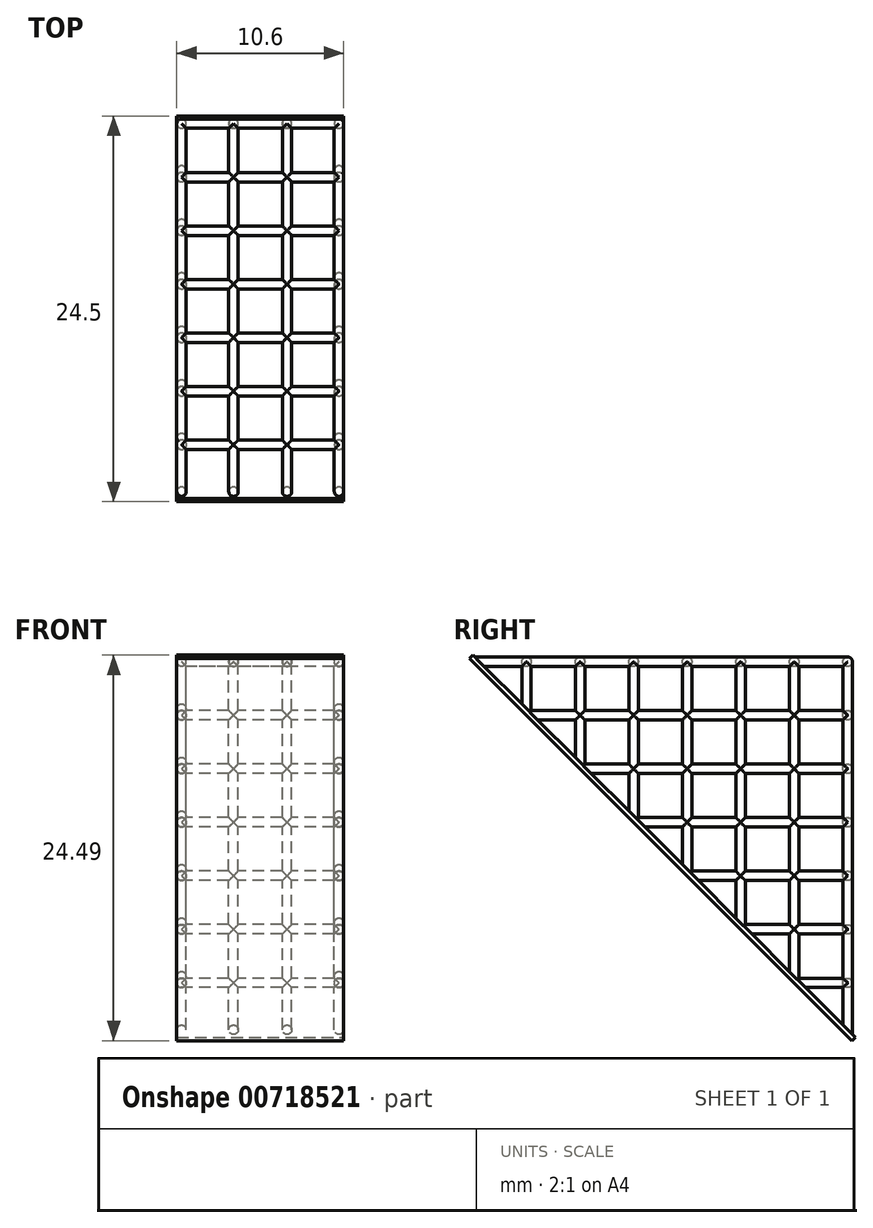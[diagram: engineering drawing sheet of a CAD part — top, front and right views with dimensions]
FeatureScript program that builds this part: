
annotation { "Feature Type Name" : "Feature", "Feature Type Description" : "" }
export const myFeature = defineFeature(function(context is Context, id is Id, definition is map)
    precondition{}
    {
        {
            var Q0;
            Q0=qCreatedBy(makeId("Top.planeOp"),FACE);
            cPlane(context, id + "F0", {"entities" : qUnion([Q0]), "cplaneType" : CPlaneType.OFFSET, "offset" : 0 * mm, "width" : 150 * mm, "height" : 150 * mm});
        }
        {
            var Q0;
            Q0=qCreatedBy(makeId("Front.planeOp"),FACE);
            cPlane(context, id + "F1", {"entities" : qUnion([Q0]), "cplaneType" : CPlaneType.OFFSET, "offset" : 0 * mm, "width" : 150 * mm, "height" : 150 * mm});
        }
        {
            assignVariable(context, id + "F2", {"variableType" : VariableType.LENGTH, "name" : "PoleD", "lengthValue" : 0.6 * mm});
        }
        {
            assignVariable(context, id + "F3", {"variableType" : VariableType.LENGTH, "name" : "PoleL", "lengthValue" : 10 * mm});
        }
        {
            assignVariable(context, id + "F4", {"variableType" : VariableType.LENGTH, "name" : "PoleL2", "lengthValue" : 23.8 * mm});
        }
        {
            var Q0;
            Q0=qCreatedBy(makeId("Right.planeOp"),FACE);
            var sketch = newSketch(context, id + "F5", { "sketchPlane" : qUnion([Q0])});
            skCircle(sketch, "E0", {"center": v(0, 0) * mm, "radius": 0.3 * mm});
            skCircle(sketch, "E1", {"center": v(3.4, 0) * mm, "radius": 0.3 * mm});
            skCircle(sketch, "E2", {"center": v(6.8, 0) * mm, "radius": 0.3 * mm});
            skCircle(sketch, "E3", {"center": v(10.2, 0) * mm, "radius": 0.3 * mm});
            skCircle(sketch, "E4", {"center": v(13.6, 0) * mm, "radius": 0.3 * mm});
            skCircle(sketch, "E5", {"center": v(17, 0) * mm, "radius": 0.3 * mm});
            skCircle(sketch, "E6", {"center": v(20.4, 0) * mm, "radius": 0.3 * mm});
            skCircle(sketch, "E7", {"center": v(23.8, 0) * mm, "radius": 0.3 * mm});
            skCircle(sketch, "E8", {"center": v(23.8, -3.4) * mm, "radius": 0.3 * mm});
            skCircle(sketch, "E9", {"center": v(23.8, -6.8) * mm, "radius": 0.3 * mm});
            skCircle(sketch, "E10", {"center": v(23.8, -10.2) * mm, "radius": 0.3 * mm});
            skCircle(sketch, "E11", {"center": v(23.8, -13.6) * mm, "radius": 0.3 * mm});
            skCircle(sketch, "E12", {"center": v(23.8, -17) * mm, "radius": 0.3 * mm});
            skCircle(sketch, "E13", {"center": v(23.8, -20.4) * mm, "radius": 0.3 * mm});
            skCircle(sketch, "E14", {"center": v(23.8, -23.8) * mm, "radius": 0.3 * mm});
            skSolve(sketch);
        }
        {
            var Q0;
            Q0 = qSketchRegion(id + "F5", true);
            extrude(context, id + "F6", {"entities" : qUnion([Q0]), "depth" : getVariable(context, 'PoleL'), "offsetDistance" : 25 * mm});
        }
        {
            var Q0;
            Q0=qCreatedBy(id+"F0.planeOp",FACE);
            var sketch = newSketch(context, id + "F7", { "sketchPlane" : qUnion([Q0])});
            skCircle(sketch, "E15", {"center": v(0, 0) * mm, "radius": 0.3 * mm});
            skCircle(sketch, "E16", {"center": v(0, 3.4) * mm, "radius": 0.3 * mm});
            skCircle(sketch, "E17", {"center": v(0, 6.8) * mm, "radius": 0.3 * mm});
            skCircle(sketch, "E18", {"center": v(0, 10.2) * mm, "radius": 0.3 * mm});
            skCircle(sketch, "E19", {"center": v(0, 13.6) * mm, "radius": 0.3 * mm});
            skCircle(sketch, "E20", {"center": v(0, 17) * mm, "radius": 0.3 * mm});
            skCircle(sketch, "E21", {"center": v(0, 20.4) * mm, "radius": 0.3 * mm});
            skCircle(sketch, "E22", {"center": v(0, 23.8) * mm, "radius": 0.3 * mm});
            skCircle(sketch, "E23", {"center": v(10, 0) * mm, "radius": 0.3 * mm});
            skCircle(sketch, "E24", {"center": v(10, 3.4) * mm, "radius": 0.3 * mm});
            skCircle(sketch, "E25", {"center": v(10, 6.8) * mm, "radius": 0.3 * mm});
            skCircle(sketch, "E26", {"center": v(10, 10.2) * mm, "radius": 0.3 * mm});
            skCircle(sketch, "E27", {"center": v(10, 13.6) * mm, "radius": 0.3 * mm});
            skCircle(sketch, "E28", {"center": v(10, 17) * mm, "radius": 0.3 * mm});
            skCircle(sketch, "E29", {"center": v(10, 20.4) * mm, "radius": 0.3 * mm});
            skCircle(sketch, "E30", {"center": v(3.3, 23.8) * mm, "radius": 0.3 * mm});
            skCircle(sketch, "E31", {"center": v(6.7, 23.8) * mm, "radius": 0.3 * mm});
            skCircle(sketch, "E32", {"center": v(10, 23.8) * mm, "radius": 0.3 * mm});
            skSolve(sketch);
        }
        {
            var Q0;
            Q0 = qSketchRegion(id + "F7", true);
            extrude(context, id + "F8", {"entities" : qUnion([Q0]), "oppositeDirection" : true, "depth" : getVariable(context, 'PoleL2'), "offsetDistance" : 25 * mm});
        }
        {
            var Q0;
            Q0=qCreatedBy(id+"F1.planeOp",FACE);
            var sketch = newSketch(context, id + "F9", { "sketchPlane" : qUnion([Q0])});
            skCircle(sketch, "E33", {"center": v(0, -23.8) * mm, "radius": 0.3 * mm});
            skCircle(sketch, "E34", {"center": v(0, -20.4) * mm, "radius": 0.3 * mm});
            skCircle(sketch, "E35", {"center": v(0, -17) * mm, "radius": 0.3 * mm});
            skCircle(sketch, "E36", {"center": v(0, -13.6) * mm, "radius": 0.3 * mm});
            skCircle(sketch, "E37", {"center": v(0, -10.2) * mm, "radius": 0.3 * mm});
            skCircle(sketch, "E38", {"center": v(0, -6.8) * mm, "radius": 0.3 * mm});
            skCircle(sketch, "E39", {"center": v(0, -3.4) * mm, "radius": 0.3 * mm});
            skCircle(sketch, "E40", {"center": v(0, 0) * mm, "radius": 0.3 * mm});
            skCircle(sketch, "E41", {"center": v(10, -23.8) * mm, "radius": 0.3 * mm});
            skCircle(sketch, "E42", {"center": v(10, -20.4) * mm, "radius": 0.3 * mm});
            skCircle(sketch, "E43", {"center": v(10, -17) * mm, "radius": 0.3 * mm});
            skCircle(sketch, "E44", {"center": v(10, -13.6) * mm, "radius": 0.3 * mm});
            skCircle(sketch, "E45", {"center": v(10, -10.2) * mm, "radius": 0.3 * mm});
            skCircle(sketch, "E46", {"center": v(10, -6.8) * mm, "radius": 0.3 * mm});
            skCircle(sketch, "E47", {"center": v(10, -3.4) * mm, "radius": 0.3 * mm});
            skCircle(sketch, "E48", {"center": v(3.3, 0) * mm, "radius": 0.3 * mm});
            skCircle(sketch, "E49", {"center": v(6.7, 0) * mm, "radius": 0.3 * mm});
            skCircle(sketch, "E50", {"center": v(10, 0) * mm, "radius": 0.3 * mm});
            skSolve(sketch);
        }
        {
            var Q0;
            Q0 = qSketchRegion(id + "F9", true);
            extrude(context, id + "F10", {"entities" : qUnion([Q0]), "oppositeDirection" : true, "depth" : getVariable(context, 'PoleL2'), "offsetDistance" : 25 * mm});
        }
        {
            var Q0;
            Q0=makeQuery(id+"F6.opExtrude","SWEPT_BODY",BODY,{"disambiguationData":[OSD([sQuery(id+"F5.wireOp",EDGE,"E6")])]});
            var Q1;
            Q1=makeQuery(id+"F6.opExtrude","SWEPT_BODY",BODY,{"disambiguationData":[OSD([sQuery(id+"F5.wireOp",EDGE,"E5")])]});
            var Q2;
            Q2=makeQuery(id+"F6.opExtrude","SWEPT_BODY",BODY,{"disambiguationData":[OSD([sQuery(id+"F5.wireOp",EDGE,"E4")])]});
            var Q3;
            Q3=makeQuery(id+"F6.opExtrude","SWEPT_BODY",BODY,{"disambiguationData":[OSD([sQuery(id+"F5.wireOp",EDGE,"E8")])]});
            var Q4;
            Q4=makeQuery(id+"F6.opExtrude","SWEPT_BODY",BODY,{"disambiguationData":[OSD([sQuery(id+"F5.wireOp",EDGE,"E3")])]});
            var Q5;
            Q5=makeQuery(id+"F6.opExtrude","SWEPT_BODY",BODY,{"disambiguationData":[OSD([sQuery(id+"F5.wireOp",EDGE,"E2")])]});
            var Q6;
            Q6=makeQuery(id+"F6.opExtrude","SWEPT_BODY",BODY,{"disambiguationData":[OSD([sQuery(id+"F5.wireOp",EDGE,"E9")])]});
            var Q7;
            Q7=makeQuery(id+"F6.opExtrude","SWEPT_BODY",BODY,{"disambiguationData":[OSD([sQuery(id+"F5.wireOp",EDGE,"E10")])]});
            var Q8;
            Q8=makeQuery(id+"F6.opExtrude","SWEPT_BODY",BODY,{"disambiguationData":[OSD([sQuery(id+"F5.wireOp",EDGE,"E11")])]});
            var Q9;
            Q9=makeQuery(id+"F6.opExtrude","SWEPT_BODY",BODY,{"disambiguationData":[OSD([sQuery(id+"F5.wireOp",EDGE,"E12")])]});
            var Q10;
            Q10=makeQuery(id+"F6.opExtrude","SWEPT_BODY",BODY,{"disambiguationData":[OSD([sQuery(id+"F5.wireOp",EDGE,"E13")])]});
            var Q11;
            Q11=makeQuery(id+"F6.opExtrude","SWEPT_BODY",BODY,{"disambiguationData":[OSD([sQuery(id+"F5.wireOp",EDGE,"E14")])]});
            var Q12;
            Q12=makeQuery(id+"F6.opExtrude","SWEPT_BODY",BODY,{"disambiguationData":[OSD([sQuery(id+"F5.wireOp",EDGE,"E1")])]});
            var Q13;
            Q13=makeQuery(id+"F8.opExtrude","SWEPT_BODY",BODY,{"disambiguationData":[OSD([sQuery(id+"F7.wireOp",EDGE,"E32")])]});
            var Q14;
            Q14=makeQuery(id+"F8.opExtrude","SWEPT_BODY",BODY,{"disambiguationData":[OSD([sQuery(id+"F7.wireOp",EDGE,"E31")])]});
            var Q15;
            Q15=makeQuery(id+"F8.opExtrude","SWEPT_BODY",BODY,{"disambiguationData":[OSD([sQuery(id+"F7.wireOp",EDGE,"E30")])]});
            var Q16;
            Q16=makeQuery(id+"F8.opExtrude","SWEPT_BODY",BODY,{"disambiguationData":[OSD([sQuery(id+"F7.wireOp",EDGE,"E29")])]});
            var Q17;
            Q17=makeQuery(id+"F8.opExtrude","SWEPT_BODY",BODY,{"disambiguationData":[OSD([sQuery(id+"F7.wireOp",EDGE,"E28")])]});
            var Q18;
            Q18=makeQuery(id+"F8.opExtrude","SWEPT_BODY",BODY,{"disambiguationData":[OSD([sQuery(id+"F7.wireOp",EDGE,"E27")])]});
            var Q19;
            Q19=makeQuery(id+"F8.opExtrude","SWEPT_BODY",BODY,{"disambiguationData":[OSD([sQuery(id+"F7.wireOp",EDGE,"E26")])]});
            var Q20;
            Q20=makeQuery(id+"F6.opExtrude","SWEPT_BODY",BODY,{"disambiguationData":[OSD([sQuery(id+"F5.wireOp",EDGE,"E0")])]});
            var Q21;
            Q21=makeQuery(id+"F8.opExtrude","SWEPT_BODY",BODY,{"disambiguationData":[OSD([sQuery(id+"F7.wireOp",EDGE,"E15")])]});
            var Q22;
            Q22=makeQuery(id+"F8.opExtrude","SWEPT_BODY",BODY,{"disambiguationData":[OSD([sQuery(id+"F7.wireOp",EDGE,"E25")])]});
            var Q23;
            Q23=makeQuery(id+"F8.opExtrude","SWEPT_BODY",BODY,{"disambiguationData":[OSD([sQuery(id+"F7.wireOp",EDGE,"E23")])]});
            var Q24;
            Q24=makeQuery(id+"F8.opExtrude","SWEPT_BODY",BODY,{"disambiguationData":[OSD([sQuery(id+"F7.wireOp",EDGE,"E24")])]});
            var Q25;
            Q25=makeQuery(id+"F8.opExtrude","SWEPT_BODY",BODY,{"disambiguationData":[OSD([sQuery(id+"F7.wireOp",EDGE,"E21")])]});
            var Q26;
            Q26=makeQuery(id+"F8.opExtrude","SWEPT_BODY",BODY,{"disambiguationData":[OSD([sQuery(id+"F7.wireOp",EDGE,"E22")])]});
            var Q27;
            Q27=makeQuery(id+"F8.opExtrude","SWEPT_BODY",BODY,{"disambiguationData":[OSD([sQuery(id+"F7.wireOp",EDGE,"E20")])]});
            var Q28;
            Q28=makeQuery(id+"F8.opExtrude","SWEPT_BODY",BODY,{"disambiguationData":[OSD([sQuery(id+"F7.wireOp",EDGE,"E19")])]});
            var Q29;
            Q29=makeQuery(id+"F8.opExtrude","SWEPT_BODY",BODY,{"disambiguationData":[OSD([sQuery(id+"F7.wireOp",EDGE,"E18")])]});
            var Q30;
            Q30=makeQuery(id+"F8.opExtrude","SWEPT_BODY",BODY,{"disambiguationData":[OSD([sQuery(id+"F7.wireOp",EDGE,"E17")])]});
            var Q31;
            Q31=makeQuery(id+"F6.opExtrude","SWEPT_BODY",BODY,{"disambiguationData":[OSD([sQuery(id+"F5.wireOp",EDGE,"E7")])]});
            var Q32;
            Q32=makeQuery(id+"F8.opExtrude","SWEPT_BODY",BODY,{"disambiguationData":[OSD([sQuery(id+"F7.wireOp",EDGE,"E16")])]});
            var Q33;
            Q33=makeQuery(id+"F10.opExtrude","SWEPT_BODY",BODY,{"disambiguationData":[OSD([sQuery(id+"F9.wireOp",EDGE,"E33")])]});
            var Q34;
            Q34=makeQuery(id+"F10.opExtrude","SWEPT_BODY",BODY,{"disambiguationData":[OSD([sQuery(id+"F9.wireOp",EDGE,"E34")])]});
            var Q35;
            Q35=makeQuery(id+"F10.opExtrude","SWEPT_BODY",BODY,{"disambiguationData":[OSD([sQuery(id+"F9.wireOp",EDGE,"E35")])]});
            var Q36;
            Q36=makeQuery(id+"F10.opExtrude","SWEPT_BODY",BODY,{"disambiguationData":[OSD([sQuery(id+"F9.wireOp",EDGE,"E36")])]});
            var Q37;
            Q37=makeQuery(id+"F10.opExtrude","SWEPT_BODY",BODY,{"disambiguationData":[OSD([sQuery(id+"F9.wireOp",EDGE,"E37")])]});
            var Q38;
            Q38=makeQuery(id+"F10.opExtrude","SWEPT_BODY",BODY,{"disambiguationData":[OSD([sQuery(id+"F9.wireOp",EDGE,"E38")])]});
            var Q39;
            Q39=makeQuery(id+"F10.opExtrude","SWEPT_BODY",BODY,{"disambiguationData":[OSD([sQuery(id+"F9.wireOp",EDGE,"E39")])]});
            var Q40;
            Q40=makeQuery(id+"F10.opExtrude","SWEPT_BODY",BODY,{"disambiguationData":[OSD([sQuery(id+"F9.wireOp",EDGE,"E40")])]});
            var Q41;
            Q41=makeQuery(id+"F10.opExtrude","SWEPT_BODY",BODY,{"disambiguationData":[OSD([sQuery(id+"F9.wireOp",EDGE,"E41")])]});
            var Q42;
            Q42=makeQuery(id+"F10.opExtrude","SWEPT_BODY",BODY,{"disambiguationData":[OSD([sQuery(id+"F9.wireOp",EDGE,"E42")])]});
            var Q43;
            Q43=makeQuery(id+"F10.opExtrude","SWEPT_BODY",BODY,{"disambiguationData":[OSD([sQuery(id+"F9.wireOp",EDGE,"E43")])]});
            var Q44;
            Q44=makeQuery(id+"F10.opExtrude","SWEPT_BODY",BODY,{"disambiguationData":[OSD([sQuery(id+"F9.wireOp",EDGE,"E44")])]});
            var Q45;
            Q45=makeQuery(id+"F10.opExtrude","SWEPT_BODY",BODY,{"disambiguationData":[OSD([sQuery(id+"F9.wireOp",EDGE,"E45")])]});
            var Q46;
            Q46=makeQuery(id+"F10.opExtrude","SWEPT_BODY",BODY,{"disambiguationData":[OSD([sQuery(id+"F9.wireOp",EDGE,"E46")])]});
            var Q47;
            Q47=makeQuery(id+"F10.opExtrude","SWEPT_BODY",BODY,{"disambiguationData":[OSD([sQuery(id+"F9.wireOp",EDGE,"E47")])]});
            var Q48;
            Q48=makeQuery(id+"F10.opExtrude","SWEPT_BODY",BODY,{"disambiguationData":[OSD([sQuery(id+"F9.wireOp",EDGE,"E48")])]});
            var Q49;
            Q49=makeQuery(id+"F10.opExtrude","SWEPT_BODY",BODY,{"disambiguationData":[OSD([sQuery(id+"F9.wireOp",EDGE,"E49")])]});
            var Q50;
            Q50=makeQuery(id+"F10.opExtrude","SWEPT_BODY",BODY,{"disambiguationData":[OSD([sQuery(id+"F9.wireOp",EDGE,"E50")])]});
            booleanBodies(context, id + "F11", {"operationType" : BooleanOperationType.UNION, "tools" : qUnion([Q0, Q1, Q2, Q3, Q4, Q5, Q6, Q7, Q8, Q9, Q10, Q11, Q12, Q13, Q14, Q15, Q16, Q17, Q18, Q19, Q20, Q21, Q22, Q23, Q24, Q25, Q26, Q27, Q28, Q29, Q30, Q31, Q32, Q33, Q34, Q35, Q36, Q37, Q38, Q39, Q40, Q41, Q42, Q43, Q44, Q45, Q46, Q47, Q48, Q49, Q50])});
        }
        {
            var Q0;
            Q0=makeQuery(id+"F8.opExtrude","CAP_FACE",FACE,{"disambiguationData":[OSD([sQuery(id+"F7.wireOp",EDGE,"E32")])],"isStart":true});
            var sketch = newSketch(context, id + "F12", { "sketchPlane" : qUnion([Q0])});
            skLineSegment(sketch, "E51", {"start": v(10, 23.8) * mm, "end": v(10, 24.35) * mm});
            skSolve(sketch);
        }
        {
            var Q0;
            Q0=makeQuery(id+"F8.opExtrude","CAP_FACE",FACE,{"disambiguationData":[OSD([sQuery(id+"F7.wireOp",EDGE,"E23")])],"isStart":true});
            var sketch = newSketch(context, id + "F13", { "sketchPlane" : qUnion([Q0])});
            skLineSegment(sketch, "E52", {"start": v(10, 0) * mm, "end": v(10, -0.38) * mm});
            skSolve(sketch);
        }
        {
            var Q0;
            {var subQ1=sQuery(id+"F7.wireOp",EDGE,"E23");var subQ2=makeQuery(id+"F8.opExtrude","CAP_EDGE",EDGE,{"disambiguationData":[OSD([subQ1])],"isStart":true});Q0=makeQuery(id+"F13.imprint","IMPRINT",FACE,{"disambiguationData":[TD([[makeQuery(id+"F13.imprint","IMPRINT",EDGE,{"derivedFrom":subQ2}),1.0]])]});}
            var Q1;
            Q1=sQuery(id+"F13.wireOp",EDGE,"E52");
            revolve(context, id + "F14", {"operationType" : NewBodyOperationType.ADD, "surfaceOperationType" : NewSurfaceOperationType.NEW, "entities" : qUnion([Q0]), "axis" : qUnion([Q1]), "revolveType" : RevolveType.FULL});
        }
        {
            var Q0;
            {var subQ1=sQuery(id+"F7.wireOp",EDGE,"E32");var subQ2=makeQuery(id+"F8.opExtrude","CAP_EDGE",EDGE,{"disambiguationData":[OSD([subQ1])],"isStart":true});Q0=makeQuery(id+"F12.imprint","IMPRINT",FACE,{"disambiguationData":[TD([[makeQuery(id+"F12.imprint","IMPRINT",EDGE,{"derivedFrom":subQ2}),1.0]])]});}
            var Q1;
            Q1=sQuery(id+"F12.wireOp",EDGE,"E51");
            revolve(context, id + "F15", {"operationType" : NewBodyOperationType.ADD, "surfaceOperationType" : NewSurfaceOperationType.NEW, "entities" : qUnion([Q0]), "axis" : qUnion([Q1]), "revolveType" : RevolveType.FULL});
        }
        {
            var Q0;
            Q0=makeQuery(id+"F8.opExtrude","CAP_FACE",FACE,{"disambiguationData":[OSD([sQuery(id+"F7.wireOp",EDGE,"E22")])],"isStart":true});
            var sketch = newSketch(context, id + "F16", { "sketchPlane" : qUnion([Q0])});
            skLineSegment(sketch, "E53", {"start": v(0, 23.8) * mm, "end": v(0, 24.59) * mm});
            skSolve(sketch);
        }
        {
            var Q0;
            Q0=makeQuery(id+"F6.opExtrude","CAP_FACE",FACE,{"disambiguationData":[OSD([sQuery(id+"F5.wireOp",EDGE,"E7")])],"isStart":true});
            var Q1;
            Q1=sQuery(id+"F16.wireOp",EDGE,"E53");
            revolve(context, id + "F17", {"operationType" : NewBodyOperationType.ADD, "surfaceOperationType" : NewSurfaceOperationType.NEW, "entities" : qUnion([Q0]), "axis" : qUnion([Q1]), "revolveType" : RevolveType.FULL});
        }
        {
            var Q0;
            Q0=makeQuery(id+"F10.opExtrude","CAP_FACE",FACE,{"disambiguationData":[OSD([sQuery(id+"F9.wireOp",EDGE,"E33")])],"isStart":false});
            var sketch = newSketch(context, id + "F18", { "sketchPlane" : qUnion([Q0])});
            skLineSegment(sketch, "E54", {"start": v(0, -23.8) * mm, "end": v(0.65, -23.8) * mm});
            skLineSegment(sketch, "E55", {"start": v(0.65, -23.8) * mm, "end": v(-11.19, -23.8) * mm});
            skSolve(sketch);
        }
        {
            var Q0;
            Q0=makeQuery(id+"F8.opExtrude","CAP_FACE",FACE,{"disambiguationData":[OSD([sQuery(id+"F7.wireOp",EDGE,"E32")])],"isStart":false});
            var Q1;
            Q1=sQuery(id+"F18.wireOp",EDGE,"E55");
            revolve(context, id + "F19", {"operationType" : NewBodyOperationType.ADD, "surfaceOperationType" : NewSurfaceOperationType.NEW, "entities" : qUnion([Q0]), "axis" : qUnion([Q1]), "revolveType" : RevolveType.FULL});
        }
        {
            var Q0;
            Q0=makeQuery(id+"F8.opExtrude","CAP_FACE",FACE,{"disambiguationData":[OSD([sQuery(id+"F7.wireOp",EDGE,"E22")])],"isStart":false});
            var Q1;
            Q1=makeQuery(id+"F11.opBoolean","INTERSECT",EDGE,{"derivedFrom":[makeQuery(id+"F8.opExtrude","CAP_FACE",FACE,{"disambiguationData":[OSD([sQuery(id+"F7.wireOp",EDGE,"E22")])],"isStart":false}),makeQuery(id+"F10.opExtrude","CAP_FACE",FACE,{"disambiguationData":[OSD([sQuery(id+"F9.wireOp",EDGE,"E33")])],"isStart":false})]});
            revolve(context, id + "F20", {"operationType" : NewBodyOperationType.ADD, "surfaceOperationType" : NewSurfaceOperationType.NEW, "entities" : qUnion([Q0]), "axis" : qUnion([Q1]), "revolveType" : RevolveType.FULL});
        }
        {
            var Q0;
            Q0=makeQuery(id+"F6.opExtrude","CAP_FACE",FACE,{"disambiguationData":[OSD([sQuery(id+"F5.wireOp",EDGE,"E0")])],"isStart":true});
            var sketch = newSketch(context, id + "F21", { "sketchPlane" : qUnion([Q0])});
            skLineSegment(sketch, "E56", {"start": v(0, 0) * mm, "end": v(0.48, 0) * mm});
            skSolve(sketch);
        }
        {
            var Q0;
            {var subQ1=sQuery(id+"F5.wireOp",EDGE,"E0");var subQ2=makeQuery(id+"F6.opExtrude","CAP_EDGE",EDGE,{"disambiguationData":[OSD([subQ1])],"isStart":true});Q0=makeQuery(id+"F21.imprint","IMPRINT",FACE,{"disambiguationData":[TD([[makeQuery(id+"F21.imprint","IMPRINT",EDGE,{"derivedFrom":subQ2}),-1.0]])]});}
            var Q1;
            Q1=sQuery(id+"F21.wireOp",EDGE,"E56");
            revolve(context, id + "F22", {"operationType" : NewBodyOperationType.ADD, "surfaceOperationType" : NewSurfaceOperationType.NEW, "entities" : qUnion([Q0]), "axis" : qUnion([Q1]), "revolveType" : RevolveType.FULL});
        }
        {
            var Q0;
            Q0=qCreatedBy(makeId("Top.planeOp"),FACE);
            var sketch = newSketch(context, id + "F23", { "sketchPlane" : qUnion([Q0])});
            skLineSegment(sketch, "E57", {"start": v(0, 0) * mm, "end": v(2.28, 0) * mm});
            skSolve(sketch);
        }
        {
            var Q0;
            Q0=qCreatedBy(makeId("Top.planeOp"),FACE);
            var Q1;
            Q1=sQuery(id+"F23.wireOp",EDGE,"E57");
            cPlane(context, id + "F24", {"entities" : qUnion([Q0, Q1]), "cplaneType" : CPlaneType.LINE_ANGLE, "offset" : 25 * mm, "angle" : 135 * degree, "width" : 150 * mm, "height" : 150 * mm});
        }
        {
            var Q0;
            Q0=qCreatedBy(id+"F24.planeOp",FACE);
            var sketch = newSketch(context, id + "F25", { "sketchPlane" : qUnion([Q0])});
            skLineSegment(sketch, "E58.bottom", {"start": v(0.3, 0.3) * mm, "end": v(-10.3, 0.3) * mm});
            skLineSegment(sketch, "E58.top", {"start": v(0.3, -34.05) * mm, "end": v(-10.3, -34.05) * mm});
            skLineSegment(sketch, "E58.left", {"start": v(0.3, 0.3) * mm, "end": v(0.3, -34.05) * mm});
            skLineSegment(sketch, "E58.right", {"start": v(-10.3, 0.3) * mm, "end": v(-10.3, -34.05) * mm});
            skSolve(sketch);
        }
        {
            var Q0;
            Q0 = qSketchRegion(id + "F25", true);
            extrude(context, id + "F26", {"entities" : qUnion([Q0]), "operationType" : NewBodyOperationType.ADD, "depth" : getVariable(context, 'PoleD') * 0.5, "offsetDistance" : 25 * mm});
        }
        {
            var Q0;
            Q0=qCreatedBy(id+"F24.planeOp",FACE);
            var sketch = newSketch(context, id + "F27", { "sketchPlane" : qUnion([Q0])});
            skLineSegment(sketch, "E59.bottom", {"start": v(4, 4) * mm, "end": v(-14, 4) * mm});
            skLineSegment(sketch, "E59.top", {"start": v(4, -38.84) * mm, "end": v(-14, -38.84) * mm});
            skLineSegment(sketch, "E59.left", {"start": v(4, 4) * mm, "end": v(4, -38.84) * mm});
            skLineSegment(sketch, "E59.right", {"start": v(-14, 4) * mm, "end": v(-14, -38.84) * mm});
            skSolve(sketch);
        }
        {
            var Q0;
            Q0 = qSketchRegion(id + "F27", true);
            extrude(context, id + "F28", {"entities" : qUnion([Q0]), "operationType" : NewBodyOperationType.REMOVE, "oppositeDirection" : true, "depth" : 25 * mm, "offsetDistance" : 25 * mm});
        }
    });
